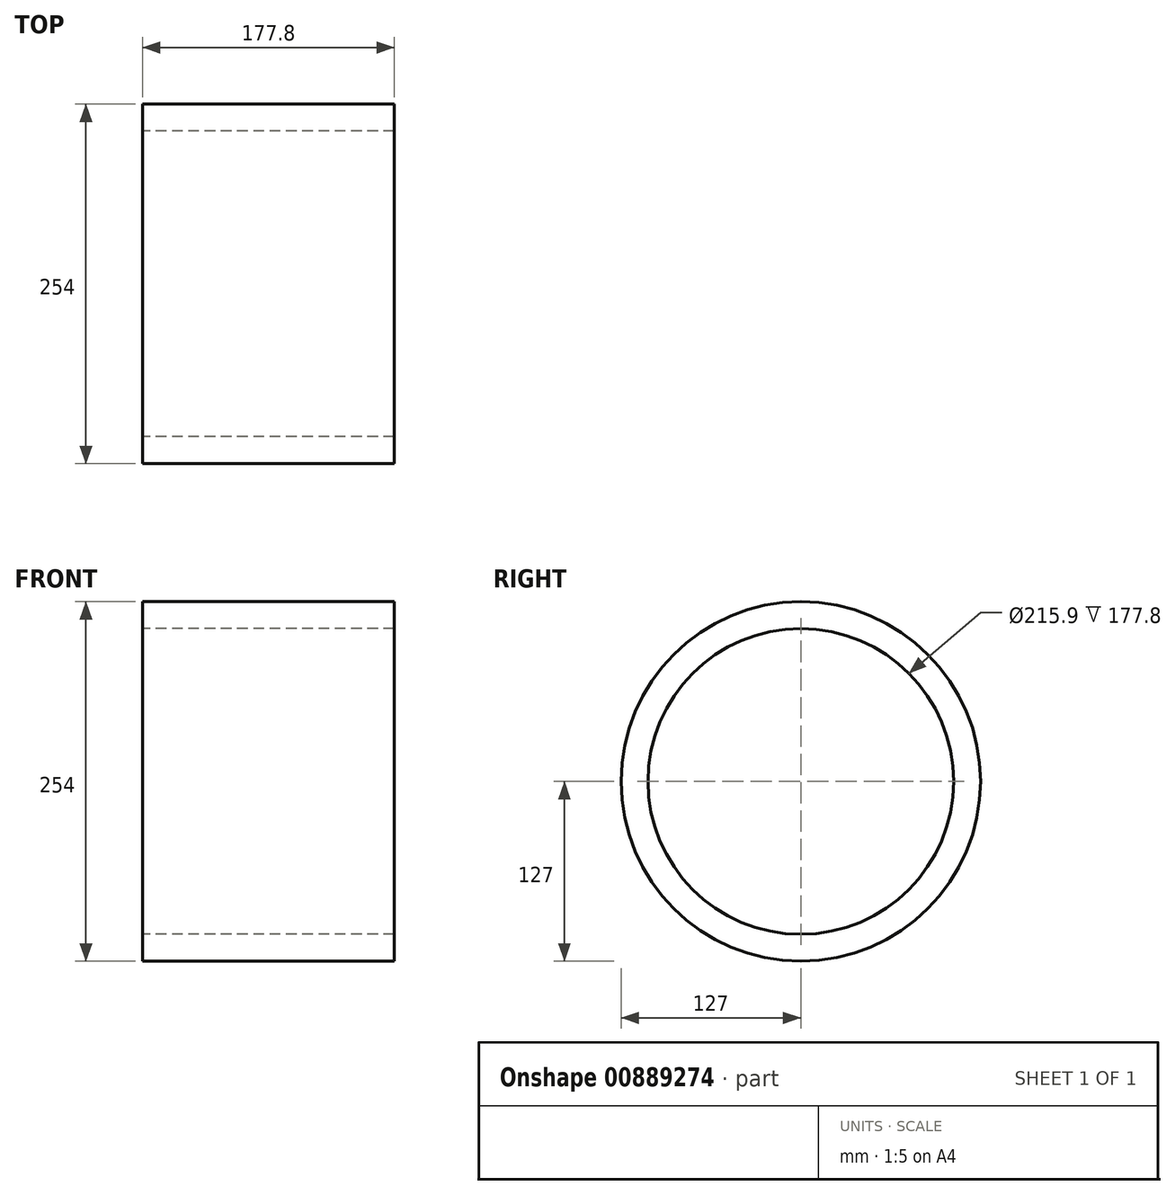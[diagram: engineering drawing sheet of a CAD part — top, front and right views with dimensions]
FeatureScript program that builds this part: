
annotation { "Feature Type Name" : "Feature", "Feature Type Description" : "" }
export const myFeature = defineFeature(function(context is Context, id is Id, definition is map)
    precondition{}
    {
        {
            var Q0;
            Q0=qCreatedBy(makeId("Right.planeOp"),FACE);
            var sketch = newSketch(context, id + "F0", { "sketchPlane" : qUnion([Q0])});
            skCircle(sketch, "E0", {"center": v(0, 0) * mm, "radius": 127 * mm});
            skCircle(sketch, "E1", {"center": v(0, 0) * mm, "radius": 107.95 * mm});
            skSolve(sketch);
        }
        {
            var Q0;
            Q0=makeQuery(id+"F0.imprint","IMPRINT",FACE,{"disambiguationData":[TD([[makeQuery(id+"F0.imprint","IMPRINT",EDGE,{"derivedFrom":sQuery(id+"F0.wireOp",EDGE,"E0")}),1.0]])]});
            extrude(context, id + "F1", {"entities" : qUnion([Q0]), "depth" : 177.8 * mm, "offsetDistance" : 25.4 * mm});
        }
    });
